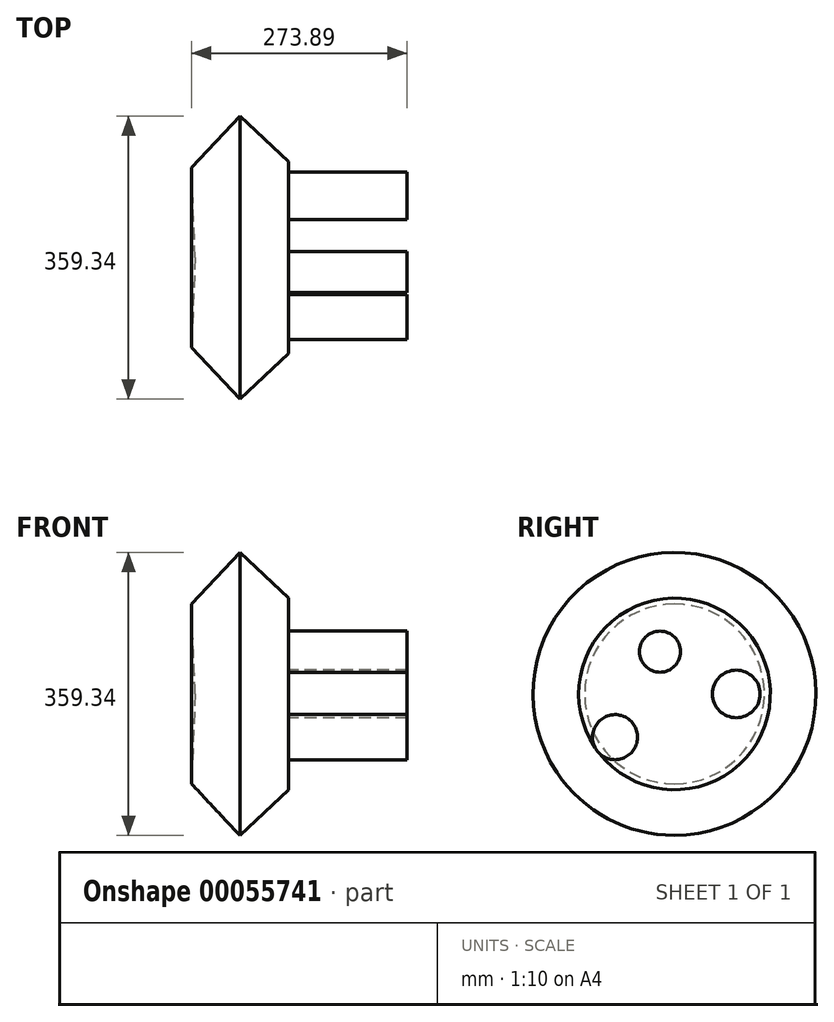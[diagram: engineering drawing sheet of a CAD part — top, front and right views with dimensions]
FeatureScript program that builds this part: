
annotation { "Feature Type Name" : "Feature", "Feature Type Description" : "" }
export const myFeature = defineFeature(function(context is Context, id is Id, definition is map)
    precondition{}
    {
        {
            var Q0;
            Q0=qCreatedBy(makeId("Top.planeOp"),FACE);
            var sketch = newSketch(context, id + "F0", { "sketchPlane" : qUnion([Q0])});
            skLineSegment(sketch, "E0", {"start": v(-61.4, 0) * mm, "end": v(61.85, 0) * mm});
            skLineSegment(sketch, "E1", {"start": v(61.85, 0) * mm, "end": v(61.85, 69.63) * mm});
            skLineSegment(sketch, "E2", {"start": v(61.85, 69.63) * mm, "end": v(-56.73, 69.63) * mm});
            skLineSegment(sketch, "E3", {"start": v(-56.73, 69.63) * mm, "end": v(-61.4, -44.53) * mm});
            skLineSegment(sketch, "E4", {"start": v(-61.4, -44.53) * mm, "end": v(0, -110.04) * mm});
            skLineSegment(sketch, "E5", {"start": v(0, -110.04) * mm, "end": v(61.85, -52.06) * mm});
            skLineSegment(sketch, "E6", {"start": v(61.85, -52.06) * mm, "end": v(61.85, 0) * mm});
            skSolve(sketch);
        }
        {
            var Q0;
            Q0 = qSketchRegion(id + "F0", true);
            var Q1;
            Q1=sQuery(id+"F0.wireOp",EDGE,"E2");
            revolve(context, id + "F1", {"entities" : qUnion([Q0]), "axis" : qUnion([Q1]), "revolveType" : RevolveType.FULL});
        }
        {
            var Q0;
            Q0=makeQuery(id+"F1.opRevolve","SWEPT_FACE",FACE,{"disambiguationData":[OSD([sQuery(id+"F0.wireOp",EDGE,"E1"),sQuery(id+"F0.wireOp",EDGE,"E6")])]});
            var sketch = newSketch(context, id + "F2", { "sketchPlane" : qUnion([Q0])});
            skCircle(sketch, "E7", {"center": v(148.12, 0) * mm, "radius": 30.25 * mm});
            skCircle(sketch, "E8", {"center": v(-5.9, -54.89) * mm, "radius": 28.63 * mm});
            skCircle(sketch, "E9", {"center": v(51.34, 53.7) * mm, "radius": 26.07 * mm});
            skSolve(sketch);
        }
        {
            var Q0;
            Q0 = qSketchRegion(id + "F2", true);
            extrude(context, id + "F3", {"entities" : qUnion([Q0]), "operationType" : NewBodyOperationType.ADD, "depth" : 150.63 * mm});
        }
    });
